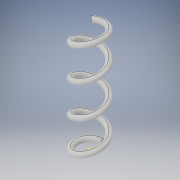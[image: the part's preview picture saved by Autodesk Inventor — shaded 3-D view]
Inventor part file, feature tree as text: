
AUTODESK INVENTOR PART (.ipt)
format: ipt  version: 2019 (Build 230136000, 136)  size: 334,336 bytes
history: native  units: in
note: dims shown in document units (in); Inventor stores cm internally (conversion verified against a paired STEP export)
features: other x8, sketch x2, helix x1
ambient origin geometry x8: Origin, YZ Plane, XZ Plane, XY Plane, X Axis, Y Axis, Z Axis, Center Point
bodies: Body1 (feature_tree)
feature tree (11):
  other  "Table"
  other  "Member = Part1-01"
  other  "Member = Part1-02"
  other  "Member = Part1-03"
  other  "Member = Part1-04"
  other  "Member = Part1-05"
  other  "Member = Part1-06"
  other  "Member = noSupTest"
  sketch  "Sketch2"  dims[d14=1.5in]
  sketch  "Sketch3"  dims[d16=0.0in d17=0.6871in d18=0.6871in d19=0.6871in d20=0.6871in]
  helix  "Coil2"  [1 undecoded]
note: 1 required parameter value undecoded (feature->parameter linkage not recoverable at this tier; creation-order binding heuristic only, values carry confidence <= 0.55)
